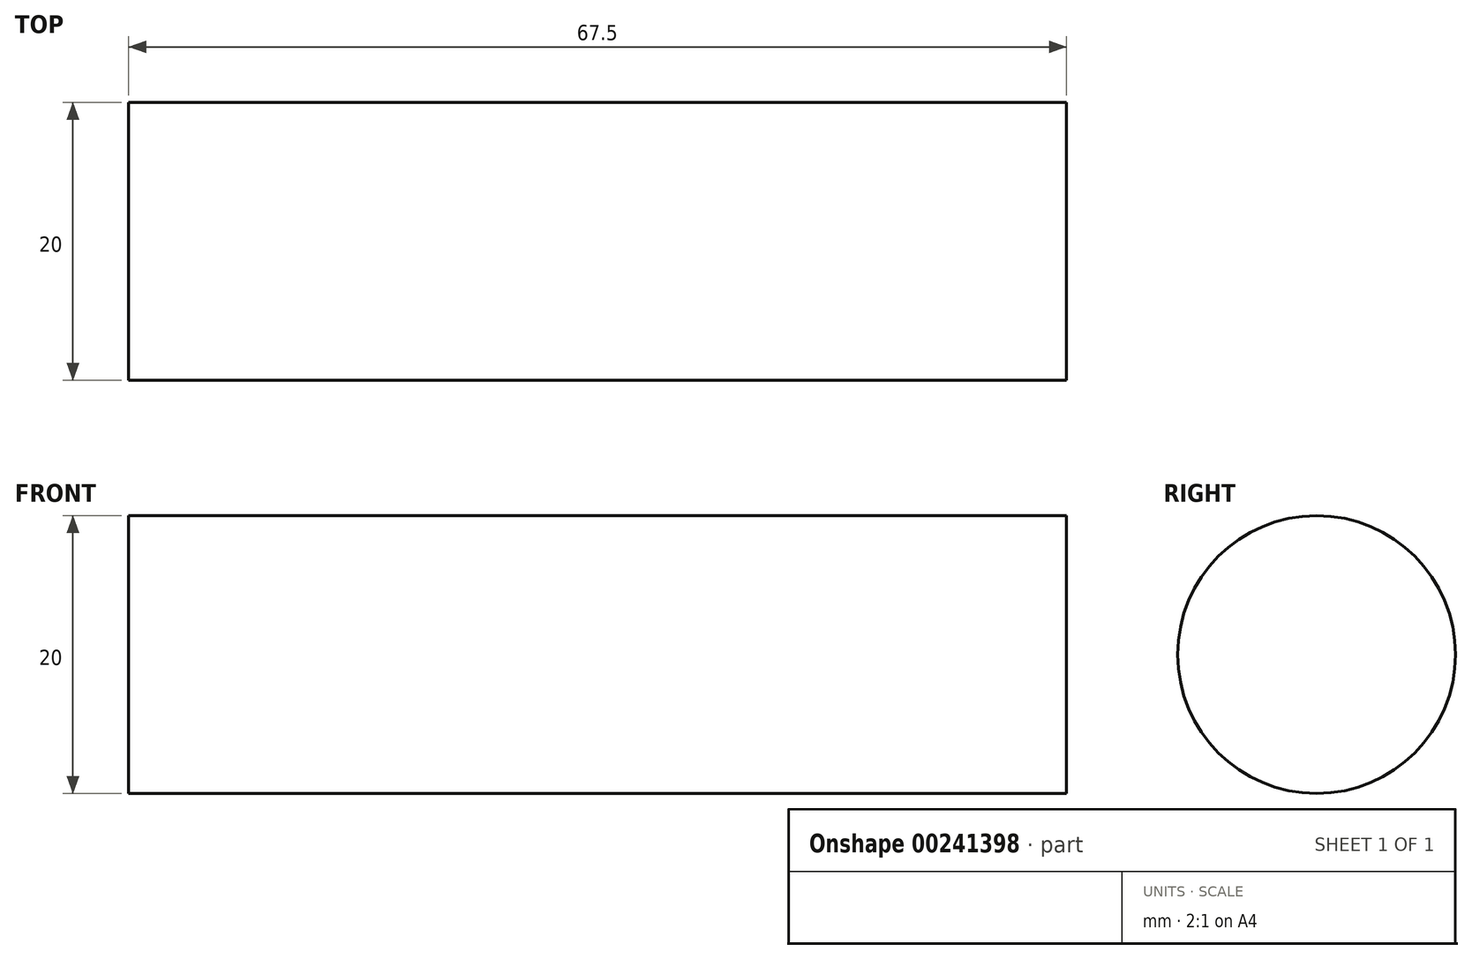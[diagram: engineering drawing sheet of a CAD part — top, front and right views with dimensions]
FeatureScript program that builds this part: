
annotation { "Feature Type Name" : "Feature", "Feature Type Description" : "" }
export const myFeature = defineFeature(function(context is Context, id is Id, definition is map)
    precondition{}
    {
        {
            var Q0;
            Q0=qCreatedBy(makeId("Right.planeOp"),FACE);
            var sketch = newSketch(context, id + "F0", { "sketchPlane" : qUnion([Q0])});
            skCircle(sketch, "E0", {"center": v(0, 0) * mm, "radius": 10 * mm});
            skSolve(sketch);
        }
        {
            var Q0;
            Q0 = qSketchRegion(id + "F0", true);
            extrude(context, id + "F1", {"entities" : qUnion([Q0]), "depth" : 67.5 * mm});
        }
    });
